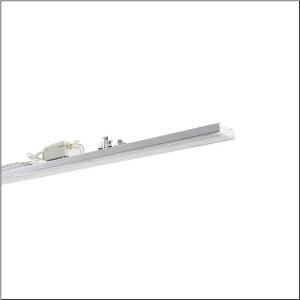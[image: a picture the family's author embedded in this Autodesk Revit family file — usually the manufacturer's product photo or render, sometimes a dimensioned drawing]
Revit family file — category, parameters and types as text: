
# Revit family: licross_11_recessed_ho_51te11cn4c5s
name_source: partatom
category: Lighting Fixtures
units: mm (PartAtom-declared; Revit-internal decimal feet)

## family parameters
Cut with Voids When Loaded = No
Host = Face
Light Source = No
Part Type = Normal
Room Calculation Point = No
Round Connector Dimension = Use Diameter
Shared = No

## types (1)
- --- (1 x LED, 12710 lm, 66.5 W, 4000K)
    Apparent Load = 67 VA
    CIE Flux Codes = 87 95 99 100 100
    Color Rendering = 80
    Color Temperature = 4000K
    Default Elevation = 1800 mm
    Description = Licross 11 Recessed HO, luminaire insert, of sheet steel, galvanised, coil coated, white, length: 1.500mm, width: 66mm, height: 67mm, LED rated luminous flux: 12.710lm, light colour: 840, SDCM (Standard Deviation of Colour Matching)MacAdam ≤ 2 SDCM (initial), control gear: ON/OFF Multilumen, CLOi, with plug, 3-pole, with phase selection, mains connection: 220..240V, AC, 50/60Hz, start of lifetime: 67W, end of service life: 75W, internal wiring halogen-free, primary light control with lens, of plastic, primary optical cover: cover, of PMMA, light emission: direct distribution, primary light characteristic: symmetric, protection rating (complete): IP54, insulation class (complete): insulation class I (protective earthing), certification: CE, ENEC, VDE, UKCA, protection symbol: D if used in an environment with non-conductive dust loads with corresponding accessories, impact resistance: IK06, permissible ambient temperature for indoor applications: -35..+35°C, corresponds to IFS (International Featured Standards) requirements for safety and quality in the food industry, reducing of maximum allowable ambient temperature of 5°C with ceiling mounting, LABS conformity tested according to VDMA 24364:2018-05, The light source and the operating device comply with the requirements of the Ecodesign Regulation (EU) 2019/2020 and are replaceable in accordance with this regulation, packaging unit: 1 piece
    Height = 58 mm
    Lamp = 1 x LED
    Lamp Light Flux = 12710 lm
    Lamp Power = 66.5 W
    Lamp count = 1
    Length = 1500 mm
    Luminous efficacy = 191 lm/W
    Manufacturer = Siteco
    ModVariant = No
    Model = 51TE11CN4C5S
    Mounting Place = Ceiling
    Mounting Type = Pendant
    Number of Poles = 1
    OnlyDefault = Yes
    Power Factor = 1
    Product Name = Licross 11 Recessed HO
    Product group = luminaire insert | ceiling pendant
    ProductGroupID = 901
    Protection Class = Protection class I
    Protection Degree = IP 54
    RLX_Detail_Level = 1
    RLX_Emergency_Light_Flux = 0 lm
    RLX_Emergency_Type = 0
    RLX_Emergency_Type_DB = No
    RlxData = <blob elided: 22553 chars, md5=6c9b1d06>
    Socket = socket
    Standby Power = 0 W
    System Light Flux = 12710 lm
    System Power = 67 W
    Type Comments = factory setting: luminous flux: 100 % | (A | C | E) | 156 mA
    Type Image = l_1296930.jpg
    URL = http://relux.com
    VarID = @adj_001531
    Voltage = 0 V
    Weight = 0.00 kg
    Width = 66 mm

## geometry (parser evidence)
native form markers: Blend x4, Sweep x10
no freeform markers — native parametric forms only
